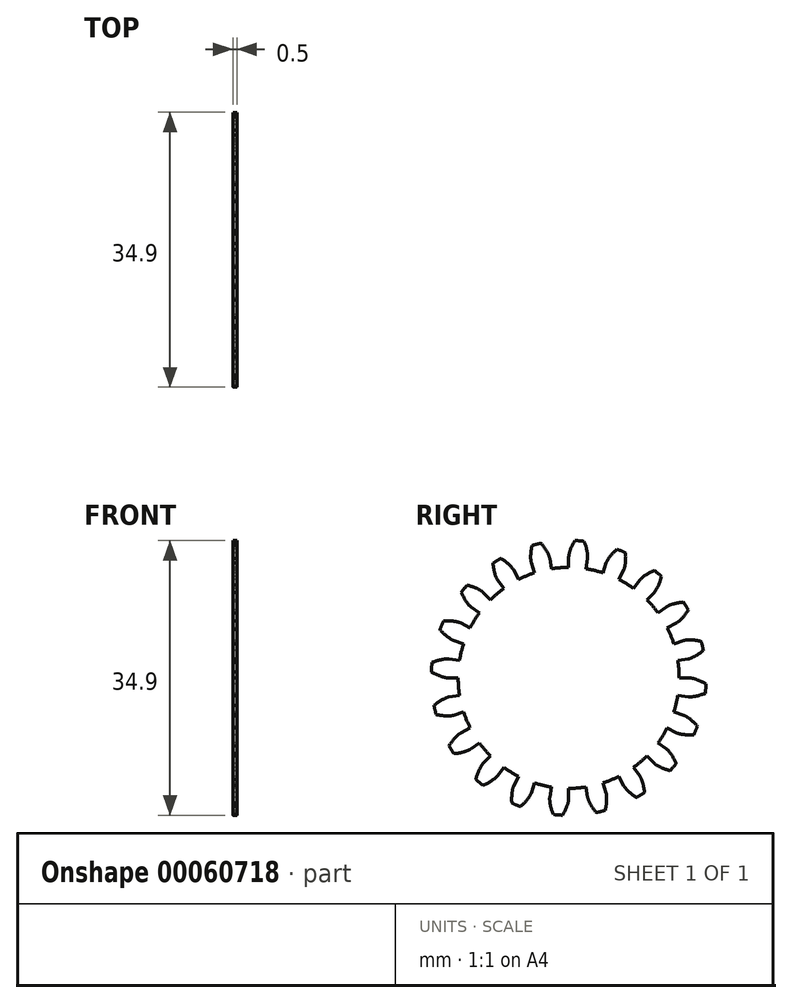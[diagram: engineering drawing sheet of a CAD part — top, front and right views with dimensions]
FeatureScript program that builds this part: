
annotation { "Feature Type Name" : "Feature", "Feature Type Description" : "" }
export const myFeature = defineFeature(function(context is Context, id is Id, definition is map)
    precondition{}
    {
        {
            assignVariable(context, id + "F0", {"name" : "NumberTeeth", "anyValue" : 20});
        }
        {
            assignVariable(context, id + "F1", {"name" : "GearThickness", "anyValue" : .5});
        }
        {
            var Q0;
            Q0=qCreatedBy(makeId("Right.planeOp"),FACE);
            var sketch = newSketch(context, id + "F2", { "sketchPlane" : qUnion([Q0])});
            skCircle(sketch, "E0", {"center": v(0, 0) * mm, "radius": 14.04 * mm});
            skCircle(sketch, "E1", {"center": v(0, 0) * mm, "radius": 15.37 * mm, "construction": true});
            skCircle(sketch, "E2", {"center": v(0, 0) * mm, "radius": 15.88 * mm, "construction": true});
            skCircle(sketch, "E3", {"center": v(0, 0) * mm, "radius": 17.46 * mm});
            skLineSegment(sketch, "E4", {"start": v(0, 0) * mm, "end": v(-15.37, 0) * mm, "construction": true});
            skLineSegment(sketch, "E5.1.0", {"start": v(0, 0) * mm, "end": v(-15.35, 0.77) * mm, "construction": true});
            skLineSegment(sketch, "E5.2.0", {"start": v(0, 0) * mm, "end": v(-15.3, 1.53) * mm, "construction": true});
            skLineSegment(sketch, "E5.3.0", {"start": v(0, 0) * mm, "end": v(-15.2, 2.3) * mm, "construction": true});
            skLineSegment(sketch, "E5.4.0", {"start": v(0, 0) * mm, "end": v(-15.06, 3.05) * mm, "construction": true});
            skLineSegment(sketch, "E5.5.0", {"start": v(0, 0) * mm, "end": v(-14.9, 3.8) * mm, "construction": true});
            skLineSegment(sketch, "E5.6.0", {"start": v(0, 0) * mm, "end": v(-14.68, 4.54) * mm, "construction": true});
            skLineSegment(sketch, "E5.7.0", {"start": v(0, 0) * mm, "end": v(-14.44, 5.27) * mm, "construction": true});
            skLineSegment(sketch, "E5.8.0", {"start": v(0, 0) * mm, "end": v(-14.16, 5.99) * mm, "construction": true});
            skLineSegment(sketch, "E5.9.0", {"start": v(0, 0) * mm, "end": v(-13.84, 6.69) * mm, "construction": true});
            skLineSegment(sketch, "E5.10.0", {"start": v(0, 0) * mm, "end": v(-13.49, 7.37) * mm, "construction": true});
            skLineSegment(sketch, "E5.11.0", {"start": v(0, 0) * mm, "end": v(-13.1, 8.03) * mm, "construction": true});
            skLineSegment(sketch, "E5.12.0", {"start": v(0, 0) * mm, "end": v(-12.68, 8.68) * mm, "construction": true});
            skLineSegment(sketch, "E5.13.0", {"start": v(0, 0) * mm, "end": v(-12.24, 9.3) * mm, "construction": true});
            skLineSegment(sketch, "E5.14.0", {"start": v(0, 0) * mm, "end": v(-11.76, 9.9) * mm, "construction": true});
            skLineSegment(sketch, "E5.anchor2", {"start": v(0, 0) * mm, "end": v(-11.76, 9.9) * mm, "construction": true});
            skLineSegment(sketch, "E6", {"start": v(-15.35, 0.77) * mm, "end": v(-15.39, 0) * mm, "construction": true});
            skLineSegment(sketch, "E7", {"start": v(-15.3, 1.53) * mm, "end": v(-15.45, 0) * mm, "construction": true});
            skLineSegment(sketch, "E8", {"start": v(-15.2, 2.3) * mm, "end": v(-15.54, 0.02) * mm, "construction": true});
            skLineSegment(sketch, "E9", {"start": v(-14.9, 3.8) * mm, "end": v(-15.84, 0.08) * mm, "construction": true});
            skLineSegment(sketch, "E10", {"start": v(-14.68, 4.54) * mm, "end": v(-16.05, 0.14) * mm, "construction": true});
            skLineSegment(sketch, "E11", {"start": v(-14.44, 5.27) * mm, "end": v(-16.28, 0.22) * mm, "construction": true});
            skLineSegment(sketch, "E12", {"start": v(-14.16, 5.99) * mm, "end": v(-16.55, 0.32) * mm, "construction": true});
            skLineSegment(sketch, "E13", {"start": v(-13.84, 6.69) * mm, "end": v(-16.85, 0.46) * mm, "construction": true});
            skLineSegment(sketch, "E14", {"start": v(-13.49, 7.37) * mm, "end": v(-17.17, 0.62) * mm, "construction": true});
            skLineSegment(sketch, "E15", {"start": v(-13.1, 8.03) * mm, "end": v(-17.52, 0.83) * mm, "construction": true});
            skLineSegment(sketch, "E16", {"start": v(-15.06, 3.05) * mm, "end": v(-15.67, 0.04) * mm, "construction": true});
            skLineSegment(sketch, "E17", {"start": v(-12.68, 8.68) * mm, "end": v(-17.9, 1.07) * mm, "construction": true});
            skLineSegment(sketch, "E18", {"start": v(-12.24, 9.3) * mm, "end": v(-18.28, 1.35) * mm, "construction": true});
            skLineSegment(sketch, "E19", {"start": v(-11.76, 9.9) * mm, "end": v(-18.69, 1.67) * mm, "construction": true});
            skLineSegment(sketch, "E20", {"start": v(0, 0) * mm, "end": v(-15.32, 1.2) * mm, "construction": true});
            skLineSegment(sketch, "E21", {"start": v(-14.04, 0) * mm, "end": v(-15.37, 0) * mm});
            skLineSegment(sketch, "E22.MirrorCS", {"start": v(-13.87, 2.2) * mm, "end": v(-15.18, 2.4) * mm});
            skFitSpline(sketch, "E23", {"points": [v(-15.37, 0) * mm, v(-15.39, 0) * mm, v(-15.45, 0) * mm, v(-15.54, 0.02) * mm, v(-15.67, 0.04) * mm, v(-15.84, 0.08) * mm, v(-16.05, 0.14) * mm, v(-16.28, 0.22) * mm, v(-16.55, 0.32) * mm, v(-16.85, 0.46) * mm, v(-17.17, 0.62) * mm, v(-17.52, 0.83) * mm, v(-17.9, 1.07) * mm, v(-18.28, 1.35) * mm, v(-18.69, 1.67) * mm], "startDerivative": vector(-0.82, 0) * mm, "endDerivative": vector(-1.2, 1) * mm});
            skLineSegment(sketch, "E24", {"start": v(-18.69, 1.67) * mm, "end": v(-19.04, 1.97) * mm, "construction": true});
            skFitSpline(sketch, "E25.MirrorCS", {"points": [v(-15.18, 2.4) * mm, v(-15.2, 2.4) * mm, v(-15.26, 2.41) * mm, v(-15.35, 2.41) * mm, v(-15.49, 2.41) * mm, v(-15.66, 2.4) * mm, v(-15.87, 2.37) * mm, v(-16.12, 2.33) * mm, v(-16.4, 2.27) * mm, v(-16.71, 2.18) * mm, v(-17.06, 2.07) * mm, v(-17.43, 1.92) * mm, v(-17.84, 1.74) * mm, v(-18.27, 1.53) * mm, v(-18.72, 1.27) * mm], "startDerivative": vector(-0.8, 0.13) * mm, "endDerivative": vector(-1.34, -0.8) * mm});
            skSolve(sketch);
        }
        {
            var Q0;
            {var subQ0=sQuery(id+"F2.wireOp",EDGE,"E0");var subQ27=makeQuery(id+"F2.imprint","INTERSECT",VERTEX,{"derivedFrom":[subQ0,sQuery(id+"F2.wireOp",EDGE,"10ea1024-8cf5-41f5-a75f-a634b86921f3.10.0")]});Q0=makeQuery(id+"F2.imprint","IMPRINT",FACE,{"disambiguationData":[TD([[makeQuery(id+"F2.imprint","IMPRINT",EDGE,{"disambiguationData":[TD([[subQ27,-1.0]])],"derivedFrom":subQ0}),1.0]])]});}
            var Q1;
            {var subQ0=sQuery(id+"F2.wireOp",EDGE,"10ea1024-8cf5-41f5-a75f-a634b86921f3.1.0");Q1=makeQuery(id+"F2.imprint","IMPRINT",FACE,{"disambiguationData":[TD([[makeQuery(id+"F2.imprint","IMPRINT",EDGE,{"derivedFrom":subQ0}),-1.0]])]});}
            var Q2;
            {var subQ7=sQuery(id+"F2.wireOp",EDGE,"10ea1024-8cf5-41f5-a75f-a634b86921f3.2.0");Q2=makeQuery(id+"F2.imprint","IMPRINT",FACE,{"disambiguationData":[TD([[makeQuery(id+"F2.imprint","IMPRINT",EDGE,{"derivedFrom":subQ7}),-1.0]])]});}
            var Q3;
            {var subQ8=sQuery(id+"F2.wireOp",EDGE,"10ea1024-8cf5-41f5-a75f-a634b86921f3.3.0");Q3=makeQuery(id+"F2.imprint","IMPRINT",FACE,{"disambiguationData":[TD([[makeQuery(id+"F2.imprint","IMPRINT",EDGE,{"derivedFrom":subQ8}),-1.0]])]});}
            var Q4;
            {var subQ2=sQuery(id+"F2.wireOp",EDGE,"10ea1024-8cf5-41f5-a75f-a634b86921f3.4.0");Q4=makeQuery(id+"F2.imprint","IMPRINT",FACE,{"disambiguationData":[TD([[makeQuery(id+"F2.imprint","IMPRINT",EDGE,{"derivedFrom":subQ2}),-1.0]])]});}
            var Q5;
            {var subQ8=sQuery(id+"F2.wireOp",EDGE,"10ea1024-8cf5-41f5-a75f-a634b86921f3.5.0");Q5=makeQuery(id+"F2.imprint","IMPRINT",FACE,{"disambiguationData":[TD([[makeQuery(id+"F2.imprint","IMPRINT",EDGE,{"derivedFrom":subQ8}),-1.0]])]});}
            var Q6;
            {var subQ3=sQuery(id+"F2.wireOp",EDGE,"10ea1024-8cf5-41f5-a75f-a634b86921f3.6.0");Q6=makeQuery(id+"F2.imprint","IMPRINT",FACE,{"disambiguationData":[TD([[makeQuery(id+"F2.imprint","IMPRINT",EDGE,{"derivedFrom":subQ3}),-1.0]])]});}
            var Q7;
            {var subQ0=sQuery(id+"F2.wireOp",EDGE,"10ea1024-8cf5-41f5-a75f-a634b86921f3.7.0");Q7=makeQuery(id+"F2.imprint","IMPRINT",FACE,{"disambiguationData":[TD([[makeQuery(id+"F2.imprint","IMPRINT",EDGE,{"derivedFrom":subQ0}),-1.0]])]});}
            var Q8;
            {var subQ5=sQuery(id+"F2.wireOp",EDGE,"10ea1024-8cf5-41f5-a75f-a634b86921f3.8.0");Q8=makeQuery(id+"F2.imprint","IMPRINT",FACE,{"disambiguationData":[TD([[makeQuery(id+"F2.imprint","IMPRINT",EDGE,{"derivedFrom":subQ5}),-1.0]])]});}
            var Q9;
            {var subQ1=sQuery(id+"F2.wireOp",EDGE,"10ea1024-8cf5-41f5-a75f-a634b86921f3.9.0");Q9=makeQuery(id+"F2.imprint","IMPRINT",FACE,{"disambiguationData":[TD([[makeQuery(id+"F2.imprint","IMPRINT",EDGE,{"derivedFrom":subQ1}),-1.0]])]});}
            var Q10;
            {var subQ5=sQuery(id+"F2.wireOp",EDGE,"10ea1024-8cf5-41f5-a75f-a634b86921f3.10.0");Q10=makeQuery(id+"F2.imprint","IMPRINT",FACE,{"disambiguationData":[TD([[makeQuery(id+"F2.imprint","IMPRINT",EDGE,{"derivedFrom":subQ5}),-1.0]])]});}
            var Q11;
            {var subQ8=sQuery(id+"F2.wireOp",EDGE,"10ea1024-8cf5-41f5-a75f-a634b86921f3.11.0");Q11=makeQuery(id+"F2.imprint","IMPRINT",FACE,{"disambiguationData":[TD([[makeQuery(id+"F2.imprint","IMPRINT",EDGE,{"derivedFrom":subQ8}),-1.0]])]});}
            var Q12;
            {var subQ2=sQuery(id+"F2.wireOp",EDGE,"10ea1024-8cf5-41f5-a75f-a634b86921f3.12.0");Q12=makeQuery(id+"F2.imprint","IMPRINT",FACE,{"disambiguationData":[TD([[makeQuery(id+"F2.imprint","IMPRINT",EDGE,{"derivedFrom":subQ2}),-1.0]])]});}
            var Q13;
            {var subQ3=sQuery(id+"F2.wireOp",EDGE,"10ea1024-8cf5-41f5-a75f-a634b86921f3.13.0");Q13=makeQuery(id+"F2.imprint","IMPRINT",FACE,{"disambiguationData":[TD([[makeQuery(id+"F2.imprint","IMPRINT",EDGE,{"derivedFrom":subQ3}),-1.0]])]});}
            var Q14;
            {var subQ0=sQuery(id+"F2.wireOp",EDGE,"10ea1024-8cf5-41f5-a75f-a634b86921f3.14.0");Q14=makeQuery(id+"F2.imprint","IMPRINT",FACE,{"disambiguationData":[TD([[makeQuery(id+"F2.imprint","IMPRINT",EDGE,{"derivedFrom":subQ0}),-1.0]])]});}
            var Q15;
            {var subQ6=sQuery(id+"F2.wireOp",EDGE,"10ea1024-8cf5-41f5-a75f-a634b86921f3.15.0");Q15=makeQuery(id+"F2.imprint","IMPRINT",FACE,{"disambiguationData":[TD([[makeQuery(id+"F2.imprint","IMPRINT",EDGE,{"derivedFrom":subQ6}),-1.0]])]});}
            var Q16;
            {var subQ5=sQuery(id+"F2.wireOp",EDGE,"10ea1024-8cf5-41f5-a75f-a634b86921f3.16.0");Q16=makeQuery(id+"F2.imprint","IMPRINT",FACE,{"disambiguationData":[TD([[makeQuery(id+"F2.imprint","IMPRINT",EDGE,{"derivedFrom":subQ5}),-1.0]])]});}
            var Q17;
            {var subQ7=sQuery(id+"F2.wireOp",EDGE,"10ea1024-8cf5-41f5-a75f-a634b86921f3.17.0");Q17=makeQuery(id+"F2.imprint","IMPRINT",FACE,{"disambiguationData":[TD([[makeQuery(id+"F2.imprint","IMPRINT",EDGE,{"derivedFrom":subQ7}),-1.0]])]});}
            var Q18;
            {var subQ5=sQuery(id+"F2.wireOp",EDGE,"10ea1024-8cf5-41f5-a75f-a634b86921f3.18.0");Q18=makeQuery(id+"F2.imprint","IMPRINT",FACE,{"disambiguationData":[TD([[makeQuery(id+"F2.imprint","IMPRINT",EDGE,{"derivedFrom":subQ5}),-1.0]])]});}
            var Q19;
            {var subQ8=sQuery(id+"F2.wireOp",EDGE,"10ea1024-8cf5-41f5-a75f-a634b86921f3.19.0");Q19=makeQuery(id+"F2.imprint","IMPRINT",FACE,{"disambiguationData":[TD([[makeQuery(id+"F2.imprint","IMPRINT",EDGE,{"derivedFrom":subQ8}),-1.0]])]});}
            var Q20;
            {var subQ8=sQuery(id+"F2.wireOp",EDGE,"E21");Q20=makeQuery(id+"F2.imprint","IMPRINT",FACE,{"disambiguationData":[TD([[makeQuery(id+"F2.imprint","IMPRINT",EDGE,{"derivedFrom":subQ8}),-1.0]])]});}
            extrude(context, id + "F3", {"entities" : qUnion([Q0, Q1, Q2, Q3, Q4, Q5, Q6, Q7, Q8, Q9, Q10, Q11, Q12, Q13, Q14, Q15, Q16, Q17, Q18, Q19, Q20]), "depth" : (getVariable(context, 'GearThickness')) * mm});
        }
        {
            var Q0;
            Q0=makeQuery(id+"F3.opExtrude","SWEPT_FACE",FACE,{"disambiguationData":[OSD([sQuery(id+"F2.wireOp",EDGE,"E25.MirrorCS")])]});
            var Q1;
            Q1=makeQuery(id+"F3.opExtrude","SWEPT_FACE",FACE,{"disambiguationData":[OSD([sQuery(id+"F2.wireOp",EDGE,"E23")])]});
            var Q2;
            Q2=makeQuery(id+"F3.opExtrude","SWEPT_FACE",FACE,{"disambiguationData":[OSD([sQuery(id+"F2.wireOp",EDGE,"E3")])]});
            var Q3;
            Q3=makeQuery(id+"F3.opExtrude","SWEPT_FACE",FACE,{"disambiguationData":[OSD([sQuery(id+"F2.wireOp",EDGE,"E22.MirrorCS")])]});
            var Q4;
            Q4=makeQuery(id+"F3.opExtrude","SWEPT_FACE",FACE,{"disambiguationData":[OSD([sQuery(id+"F2.wireOp",EDGE,"E21")])]});
            var Q5;
            Q5=makeQuery(id+"F3.opExtrude","SWEPT_FACE",FACE,{"disambiguationData":[OSD([sQuery(id+"F2.wireOp",EDGE,"E0")])]});
            circularPattern(context, id + "F4", {"faces" : qUnion([Q0, Q1, Q2, Q3, Q4]), "axis" : qUnion([Q5]), "angle" : 360 * degree, "instanceCount" : getVariable(context, 'NumberTeeth'), "equalSpace" : true, "patternType" : PatternType.FACE});
        }
    });
